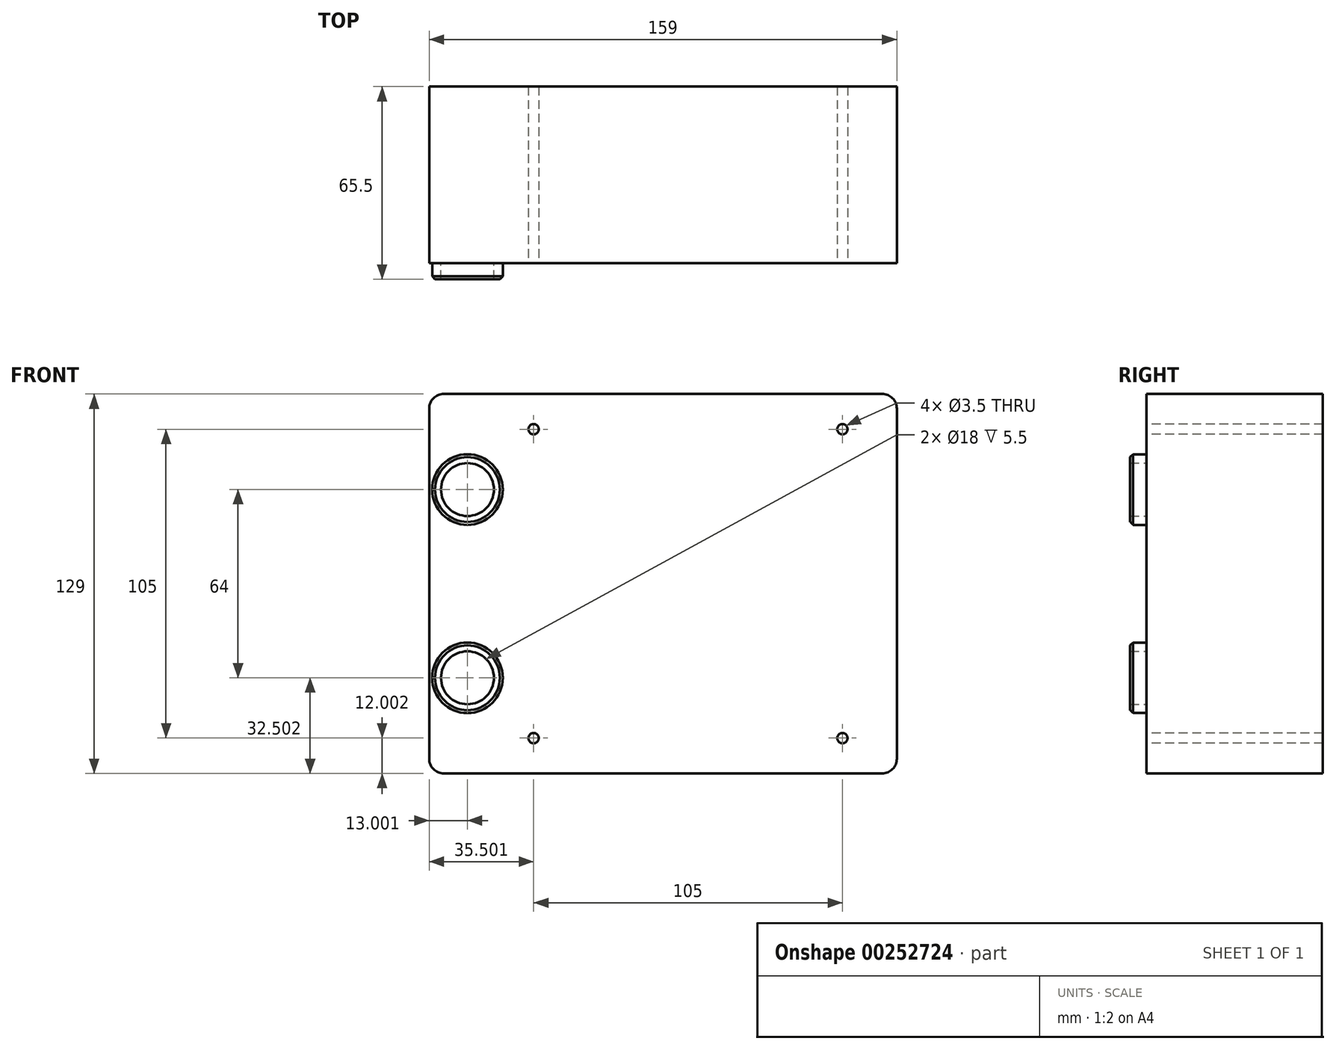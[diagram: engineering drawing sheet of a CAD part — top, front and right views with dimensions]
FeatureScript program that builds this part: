
annotation { "Feature Type Name" : "Feature", "Feature Type Description" : "" }
export const myFeature = defineFeature(function(context is Context, id is Id, definition is map)
    precondition{}
    {
        {
            var Q0;
            Q0=qCreatedBy(makeId("Front.planeOp"),FACE);
            var sketch = newSketch(context, id + "F0", { "sketchPlane" : qUnion([Q0])});
            skLineSegment(sketch, "E0.bottom", {"start": v(-74.39, 61.74) * mm, "end": v(84.61, 61.74) * mm});
            skLineSegment(sketch, "E0.top", {"start": v(-74.39, -67.26) * mm, "end": v(84.61, -67.26) * mm});
            skLineSegment(sketch, "E0.left", {"start": v(-74.39, 61.74) * mm, "end": v(-74.39, -67.26) * mm});
            skLineSegment(sketch, "E0.right", {"start": v(84.61, 61.74) * mm, "end": v(84.61, -67.26) * mm});
            skSolve(sketch);
        }
        {
            var Q0;
            Q0=makeQuery(id+"F0.imprint","IMPRINT",FACE,{"disambiguationData":[TD([[makeQuery(id+"F0.imprint","IMPRINT",EDGE,{"derivedFrom":sQuery(id+"F0.wireOp",EDGE,"E0.bottom")}),-1.0]])]});
            extrude(context, id + "F1", {"entities" : qUnion([Q0]), "depth" : 60 * mm});
        }
        {
            var Q0;
            Q0=makeQuery(id+"F1.opExtrude","CAP_FACE",FACE,{"disambiguationData":[OSD([sQuery(id+"F0.wireOp",EDGE,"E0.bottom"),sQuery(id+"F0.wireOp",EDGE,"E0.top"),sQuery(id+"F0.wireOp",EDGE,"E0.left"),sQuery(id+"F0.wireOp",EDGE,"E0.right")])],"isStart":false});
            var sketch = newSketch(context, id + "F2", { "sketchPlane" : qUnion([Q0])});
            skCircle(sketch, "E1", {"center": v(-61.39, 29.24) * mm, "radius": 12 * mm});
            skCircle(sketch, "E2", {"center": v(-61.39, -34.76) * mm, "radius": 12 * mm});
            skCircle(sketch, "E3", {"center": v(-61.39, 29.24) * mm, "radius": 9 * mm});
            skCircle(sketch, "E4", {"center": v(-61.39, -34.76) * mm, "radius": 9 * mm});
            skSolve(sketch);
        }
        {
            var Q0;
            Q0=makeQuery(id+"F2.imprint","IMPRINT",FACE,{"disambiguationData":[TD([[makeQuery(id+"F2.imprint","IMPRINT",EDGE,{"derivedFrom":sQuery(id+"F2.wireOp",EDGE,"E1")}),1.0]])]});
            var Q1;
            Q1=makeQuery(id+"F2.imprint","IMPRINT",FACE,{"disambiguationData":[TD([[makeQuery(id+"F2.imprint","IMPRINT",EDGE,{"derivedFrom":sQuery(id+"F2.wireOp",EDGE,"E2")}),1.0]])]});
            extrude(context, id + "F3", {"entities" : qUnion([Q0, Q1]), "operationType" : NewBodyOperationType.ADD, "depth" : 5.5 * mm});
        }
        {
            var Q0;
            Q0=makeQuery(id+"F1.opExtrude","SWEPT_EDGE",EDGE,{"disambiguationData":[OSD([sQuery(id+"F0.wireOp",EDGE,"E0.top"),sQuery(id+"F0.wireOp",EDGE,"E0.right")])]});
            var Q1;
            Q1=makeQuery(id+"F1.opExtrude","SWEPT_EDGE",EDGE,{"disambiguationData":[OSD([sQuery(id+"F0.wireOp",EDGE,"E0.bottom"),sQuery(id+"F0.wireOp",EDGE,"E0.right")])]});
            var Q2;
            Q2=makeQuery(id+"F1.opExtrude","SWEPT_EDGE",EDGE,{"disambiguationData":[OSD([sQuery(id+"F0.wireOp",EDGE,"E0.bottom"),sQuery(id+"F0.wireOp",EDGE,"E0.left")])]});
            var Q3;
            Q3=makeQuery(id+"F1.opExtrude","SWEPT_EDGE",EDGE,{"disambiguationData":[OSD([sQuery(id+"F0.wireOp",EDGE,"E0.top"),sQuery(id+"F0.wireOp",EDGE,"E0.left")])]});
            fillet(context, id + "F4", {"entities" : qUnion([Q0, Q1, Q2, Q3]), "radius" : 5 * mm, "tangentPropagation" : true, "allowEdgeOverflow" : false});
        }
        {
            var Q0;
            Q0=makeQuery(id+"F1.opExtrude","CAP_FACE",FACE,{"disambiguationData":[OSD([sQuery(id+"F0.wireOp",EDGE,"E0.bottom"),sQuery(id+"F0.wireOp",EDGE,"E0.top"),sQuery(id+"F0.wireOp",EDGE,"E0.left"),sQuery(id+"F0.wireOp",EDGE,"E0.right")])],"isStart":false});
            var sketch = newSketch(context, id + "F5", { "sketchPlane" : qUnion([Q0])});
            skPoint(sketch, "E5", {"position": v(-38.89, -55.26) * mm});
            skPoint(sketch, "E6", {"position": v(66.11, -55.26) * mm});
            skPoint(sketch, "E7", {"position": v(66.11, 49.74) * mm});
            skPoint(sketch, "E8", {"position": v(-38.89, 49.74) * mm});
            skSolve(sketch);
        }
        {
            var Q0;
            Q0=sQuery(id+"F5.wireOp",VERTEX,"E8");
            var Q1;
            Q1=sQuery(id+"F5.wireOp",VERTEX,"E7");
            var Q2;
            Q2=sQuery(id+"F5.wireOp",VERTEX,"E5");
            var Q3;
            Q3=sQuery(id+"F5.wireOp",VERTEX,"E6");
            var Q4;
            Q4=makeQuery(id+"F1.opExtrude","SWEPT_BODY",BODY,{"disambiguationData":[OSD([sQuery(id+"F0.wireOp",EDGE,"E0.bottom"),sQuery(id+"F0.wireOp",EDGE,"E0.top"),sQuery(id+"F0.wireOp",EDGE,"E0.left"),sQuery(id+"F0.wireOp",EDGE,"E0.right")])]});
            hole(context, id + "F6", {"style" : HoleStyle.SIMPLE, "endStyle" : HoleEndStyle.THROUGH, "holeDiameter" : 3.5 * mm, "tappedDepth" : 12 * mm, "tapClearance" : 3, "locations" : qUnion([Q0, Q1, Q2, Q3]), "scope" : qUnion([Q4])});
        }
        {
            var Q0;
            Q0=makeQuery(id+"F3.opExtrude","CAP_EDGE",EDGE,{"disambiguationData":[OSD([sQuery(id+"F2.wireOp",EDGE,"E1")])],"isStart":false});
            var Q1;
            Q1=makeQuery(id+"F3.opExtrude","CAP_EDGE",EDGE,{"disambiguationData":[OSD([sQuery(id+"F2.wireOp",EDGE,"E2")])],"isStart":false});
            chamfer(context, id + "F7", {"entities" : qUnion([Q0, Q1]), "width" : 1 * mm, "tangentPropagation" : true});
        }
    });
